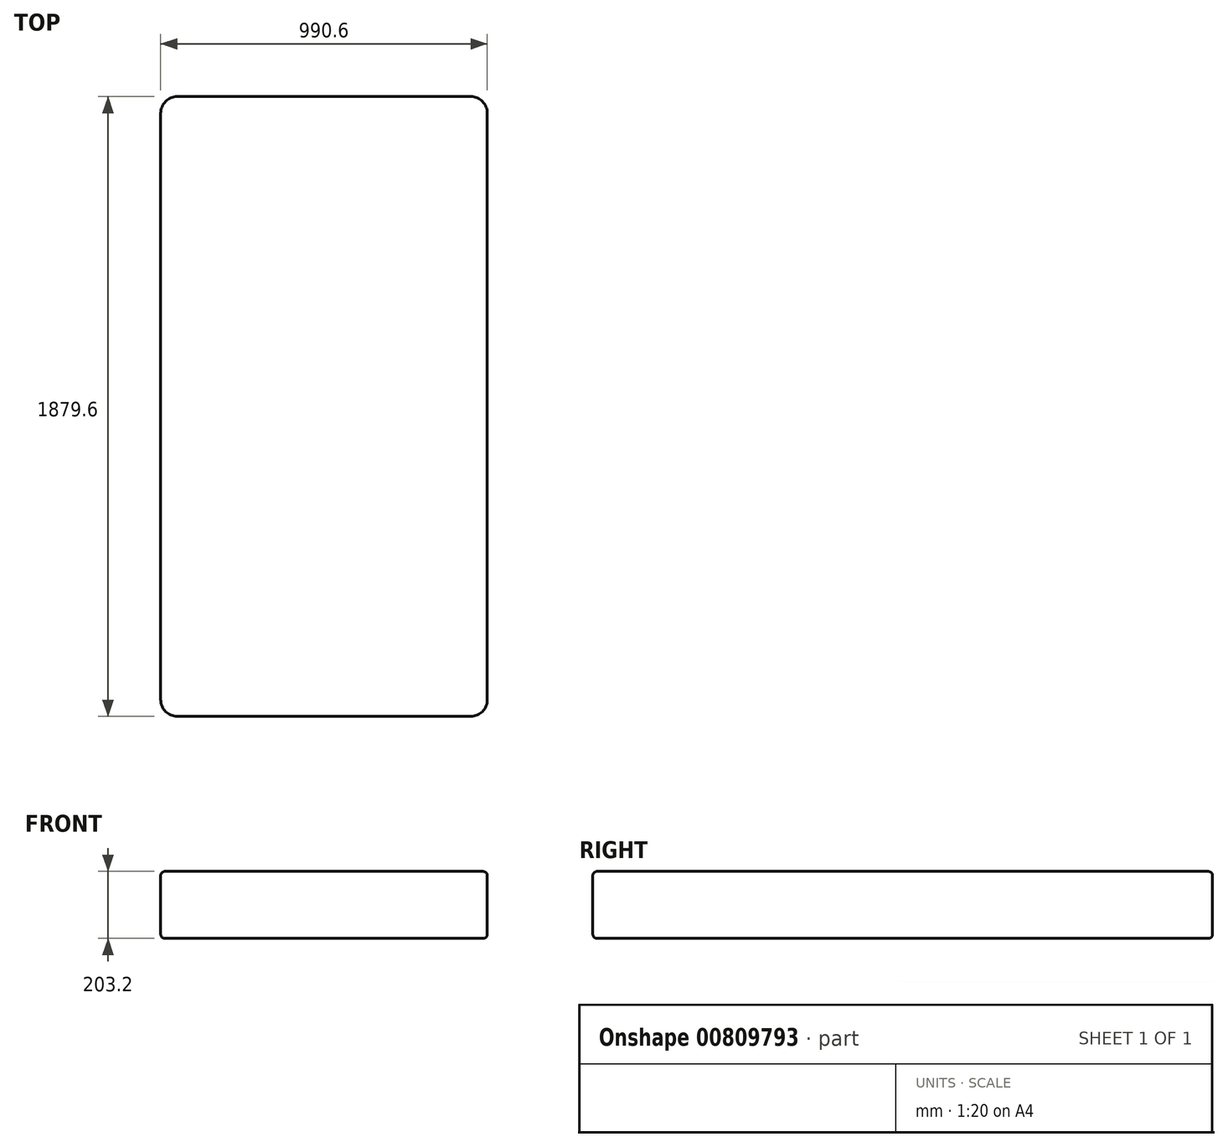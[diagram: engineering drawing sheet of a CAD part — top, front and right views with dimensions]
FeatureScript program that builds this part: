
annotation { "Feature Type Name" : "Feature", "Feature Type Description" : "" }
export const myFeature = defineFeature(function(context is Context, id is Id, definition is map)
    precondition{}
    {
        {
            var Q0;
            Q0=qCreatedBy(makeId("Top.planeOp"),FACE);
            var sketch = newSketch(context, id + "F0", { "sketchPlane" : qUnion([Q0])});
            skLineSegment(sketch, "E0.bottom", {"start": v(-495.3, 939.8) * mm, "end": v(495.3, 939.8) * mm});
            skLineSegment(sketch, "E0.top", {"start": v(-495.3, -939.8) * mm, "end": v(495.3, -939.8) * mm});
            skLineSegment(sketch, "E0.left", {"start": v(-495.3, 939.8) * mm, "end": v(-495.3, -939.8) * mm});
            skLineSegment(sketch, "E0.right", {"start": v(495.3, 939.8) * mm, "end": v(495.3, -939.8) * mm});
            skLineSegment(sketch, "E1", {"start": v(-495.3, 939.8) * mm, "end": v(495.3, -939.8) * mm, "construction": true});
            skSolve(sketch);
        }
        {
            var Q0;
            Q0=qSketchRegion(id+"F0",true);
            extrude(context, id + "F1", {"entities" : qUnion([Q0]), "depth" : 203.2 * mm, "offsetDistance" : 25.4 * mm});
        }
        {
            var Q0;
            Q0=makeQuery(id+"F1.opExtrude","CAP_EDGE",EDGE,{"disambiguationData":[OSD([sQuery(id+"F0.wireOp",EDGE,"E0.left")])],"isStart":false});
            var Q1;
            Q1=makeQuery(id+"F1.opExtrude","CAP_EDGE",EDGE,{"disambiguationData":[OSD([sQuery(id+"F0.wireOp",EDGE,"E0.top")])],"isStart":false});
            var Q2;
            Q2=makeQuery(id+"F1.opExtrude","CAP_EDGE",EDGE,{"disambiguationData":[OSD([sQuery(id+"F0.wireOp",EDGE,"E0.right")])],"isStart":false});
            var Q3;
            Q3=makeQuery(id+"F1.opExtrude","CAP_EDGE",EDGE,{"disambiguationData":[OSD([sQuery(id+"F0.wireOp",EDGE,"E0.bottom")])],"isStart":false});
            var Q4;
            Q4=makeQuery(id+"F1.opExtrude","CAP_EDGE",EDGE,{"disambiguationData":[OSD([sQuery(id+"F0.wireOp",EDGE,"E0.right")])],"isStart":true});
            var Q5;
            Q5=makeQuery(id+"F1.opExtrude","CAP_EDGE",EDGE,{"disambiguationData":[OSD([sQuery(id+"F0.wireOp",EDGE,"E0.top")])],"isStart":true});
            var Q6;
            Q6=makeQuery(id+"F1.opExtrude","CAP_EDGE",EDGE,{"disambiguationData":[OSD([sQuery(id+"F0.wireOp",EDGE,"E0.left")])],"isStart":true});
            var Q7;
            Q7=makeQuery(id+"F1.opExtrude","CAP_EDGE",EDGE,{"disambiguationData":[OSD([sQuery(id+"F0.wireOp",EDGE,"E0.bottom")])],"isStart":true});
            fillet(context, id + "F2", {"entities" : qUnion([Q0, Q1, Q2, Q3, Q4, Q5, Q6, Q7]), "radius" : 12.7 * mm, "tangentPropagation" : true, "allowEdgeOverflow" : false});
        }
        {
            var Q0;
            Q0=makeQuery(id+"F1.opExtrude","SWEPT_EDGE",EDGE,{"disambiguationData":[OSD([sQuery(id+"F0.wireOp",EDGE,"E0.top"),sQuery(id+"F0.wireOp",EDGE,"E0.left")])]});
            var Q1;
            Q1=makeQuery(id+"F1.opExtrude","SWEPT_EDGE",EDGE,{"disambiguationData":[OSD([sQuery(id+"F0.wireOp",EDGE,"E0.top"),sQuery(id+"F0.wireOp",EDGE,"E0.right")])]});
            var Q2;
            Q2=makeQuery(id+"F1.opExtrude","SWEPT_EDGE",EDGE,{"disambiguationData":[OSD([sQuery(id+"F0.wireOp",EDGE,"E0.bottom"),sQuery(id+"F0.wireOp",EDGE,"E0.right")])]});
            var Q3;
            Q3=makeQuery(id+"F1.opExtrude","SWEPT_EDGE",EDGE,{"disambiguationData":[OSD([sQuery(id+"F0.wireOp",EDGE,"E0.bottom"),sQuery(id+"F0.wireOp",EDGE,"E0.left")])]});
            fillet(context, id + "F3", {"entities" : qUnion([Q0, Q1, Q2, Q3]), "radius" : 50.8 * mm, "tangentPropagation" : true, "allowEdgeOverflow" : false});
        }
    });
